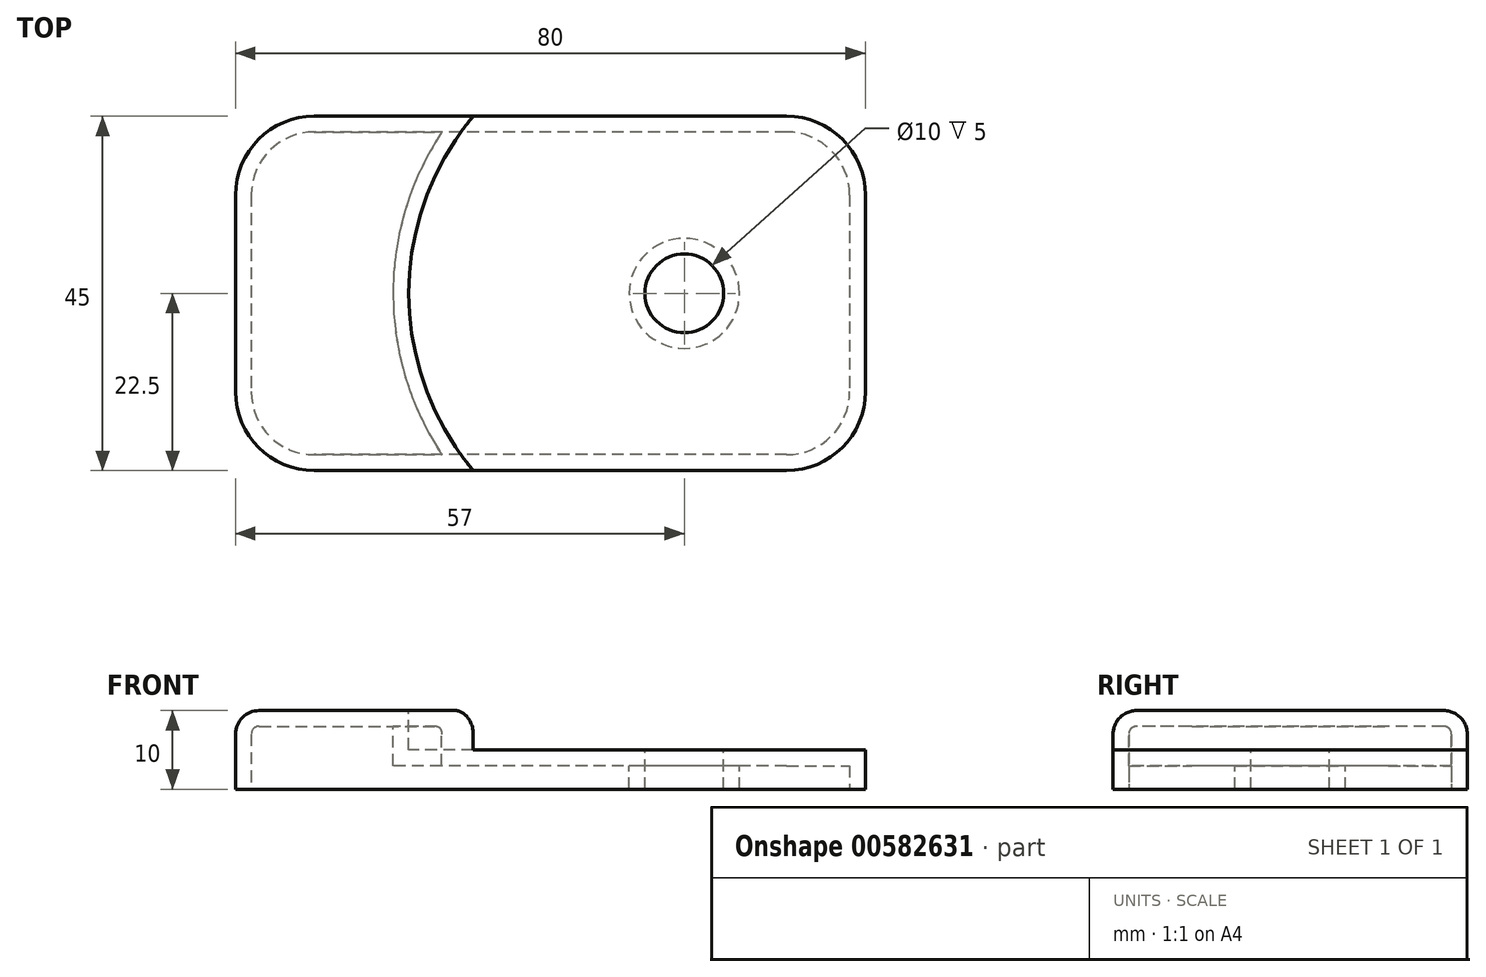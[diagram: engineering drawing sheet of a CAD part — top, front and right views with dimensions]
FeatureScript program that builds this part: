
annotation { "Feature Type Name" : "Feature", "Feature Type Description" : "" }
export const myFeature = defineFeature(function(context is Context, id is Id, definition is map)
    precondition{}
    {
        {
            var Q0;
            Q0=qCreatedBy(makeId("Top.planeOp"),FACE);
            var sketch = newSketch(context, id + "F0", { "sketchPlane" : qUnion([Q0])});
            skLineSegment(sketch, "E0.bottom", {"start": v(40, 22.5) * mm, "end": v(-40, 22.5) * mm});
            skLineSegment(sketch, "E0.top", {"start": v(40, -22.5) * mm, "end": v(-40, -22.5) * mm});
            skLineSegment(sketch, "E0.left", {"start": v(40, 22.5) * mm, "end": v(40, -22.5) * mm});
            skLineSegment(sketch, "E0.right", {"start": v(-40, 22.5) * mm, "end": v(-40, -22.5) * mm});
            skPoint(sketch, "E0.middle", {"position": v(0, 0) * mm});
            skSolve(sketch);
        }
        {
            var Q0;
            Q0=makeQuery(id+"F0.imprint","IMPRINT",FACE,{"disambiguationData":[TD([[makeQuery(id+"F0.imprint","IMPRINT",EDGE,{"derivedFrom":sQuery(id+"F0.wireOp",EDGE,"E0.bottom")}),1.0]])]});
            extrude(context, id + "F1", {"entities" : qUnion([Q0]), "depth" : 10 * mm, "offsetDistance" : 25 * mm});
        }
        {
            var Q0;
            Q0=makeQuery(id+"F1.opExtrude","CAP_EDGE",EDGE,{"disambiguationData":[OSD([sQuery(id+"F0.wireOp",EDGE,"E0.top")])],"isStart":false});
            var Q1;
            Q1=makeQuery(id+"F1.opExtrude","CAP_EDGE",EDGE,{"disambiguationData":[OSD([sQuery(id+"F0.wireOp",EDGE,"E0.right")])],"isStart":false});
            var Q2;
            Q2=makeQuery(id+"F1.opExtrude","CAP_EDGE",EDGE,{"disambiguationData":[OSD([sQuery(id+"F0.wireOp",EDGE,"E0.left")])],"isStart":false});
            var Q3;
            Q3=makeQuery(id+"F1.opExtrude","CAP_EDGE",EDGE,{"disambiguationData":[OSD([sQuery(id+"F0.wireOp",EDGE,"E0.bottom")])],"isStart":false});
            fillet(context, id + "F2", {"entities" : qUnion([Q0, Q1, Q2, Q3]), "radius" : 3 * mm, "tangentPropagation" : true, "allowEdgeOverflow" : false});
        }
        {
            var Q0;
            Q0=makeQuery(id+"F1.opExtrude","SWEPT_EDGE",EDGE,{"disambiguationData":[OSD([sQuery(id+"F0.wireOp",EDGE,"E0.top"),sQuery(id+"F0.wireOp",EDGE,"E0.right")])]});
            var Q1;
            Q1=makeQuery(id+"F1.opExtrude","SWEPT_EDGE",EDGE,{"disambiguationData":[OSD([sQuery(id+"F0.wireOp",EDGE,"E0.top"),sQuery(id+"F0.wireOp",EDGE,"E0.left")])]});
            var Q2;
            Q2=makeQuery(id+"F1.opExtrude","SWEPT_EDGE",EDGE,{"disambiguationData":[OSD([sQuery(id+"F0.wireOp",EDGE,"E0.bottom"),sQuery(id+"F0.wireOp",EDGE,"E0.left")])]});
            var Q3;
            Q3=makeQuery(id+"F1.opExtrude","SWEPT_EDGE",EDGE,{"disambiguationData":[OSD([sQuery(id+"F0.wireOp",EDGE,"E0.bottom"),sQuery(id+"F0.wireOp",EDGE,"E0.right")])]});
            fillet(context, id + "F3", {"entities" : qUnion([Q0, Q1, Q2, Q3]), "radius" : 10 * mm, "tangentPropagation" : true, "allowEdgeOverflow" : false});
        }
        {
            var Q0;
            Q0=makeQuery(id+"F1.opExtrude","CAP_FACE",FACE,{"disambiguationData":[OSD([sQuery(id+"F0.wireOp",EDGE,"E0.bottom"),sQuery(id+"F0.wireOp",EDGE,"E0.top"),sQuery(id+"F0.wireOp",EDGE,"E0.left"),sQuery(id+"F0.wireOp",EDGE,"E0.right")])],"isStart":false});
            var sketch = newSketch(context, id + "F4", { "sketchPlane" : qUnion([Q0])});
            skCircle(sketch, "E1", {"center": v(17, 0) * mm, "radius": 35 * mm});
            skLineSegment(sketch, "E2", {"start": v(17, 0) * mm, "end": v(40, 0) * mm, "construction": true});
            skSolve(sketch);
        }
        {
            var Q0;
            Q0 = qSketchRegion(id + "F4", true);
            extrude(context, id + "F5", {"entities" : qUnion([Q0]), "operationType" : NewBodyOperationType.REMOVE, "oppositeDirection" : true, "depth" : 5 * mm, "offsetDistance" : 25 * mm});
        }
        {
            var Q0;
            Q0=makeQuery(id+"F5.boolean.opBoolean","COPY",FACE,{"derivedFrom":makeQuery(id+"F5.opExtrude","CAP_FACE",FACE,{"disambiguationData":[OSD([sQuery(id+"F4.wireOp",EDGE,"E1")])],"isStart":false})});
            var sketch = newSketch(context, id + "F6", { "sketchPlane" : qUnion([Q0])});
            skLineSegment(sketch, "E3", {"start": v(40, 0) * mm, "end": v(17, 0) * mm, "construction": true});
            skPoint(sketch, "E3.endSnap0", {"position": v(40, 0) * mm});
            skCircle(sketch, "E4", {"center": v(17, 0) * mm, "radius": 5 * mm});
            skSolve(sketch);
        }
        {
            var Q0;
            Q0 = qSketchRegion(id + "F6", true);
            extrude(context, id + "F7", {"entities" : qUnion([Q0]), "operationType" : NewBodyOperationType.REMOVE, "oppositeDirection" : true, "depth" : 10 * mm, "offsetDistance" : 25 * mm});
        }
        {
            var Q0;
            Q0=makeQuery(id+"F1.opExtrude","CAP_FACE",FACE,{"disambiguationData":[OSD([sQuery(id+"F0.wireOp",EDGE,"E0.bottom"),sQuery(id+"F0.wireOp",EDGE,"E0.top"),sQuery(id+"F0.wireOp",EDGE,"E0.left"),sQuery(id+"F0.wireOp",EDGE,"E0.right")])],"isStart":true});
            shell(context, id + "F8", {"entities" : qUnion([Q0]), "thickness" : 2 * mm});
        }
    });
